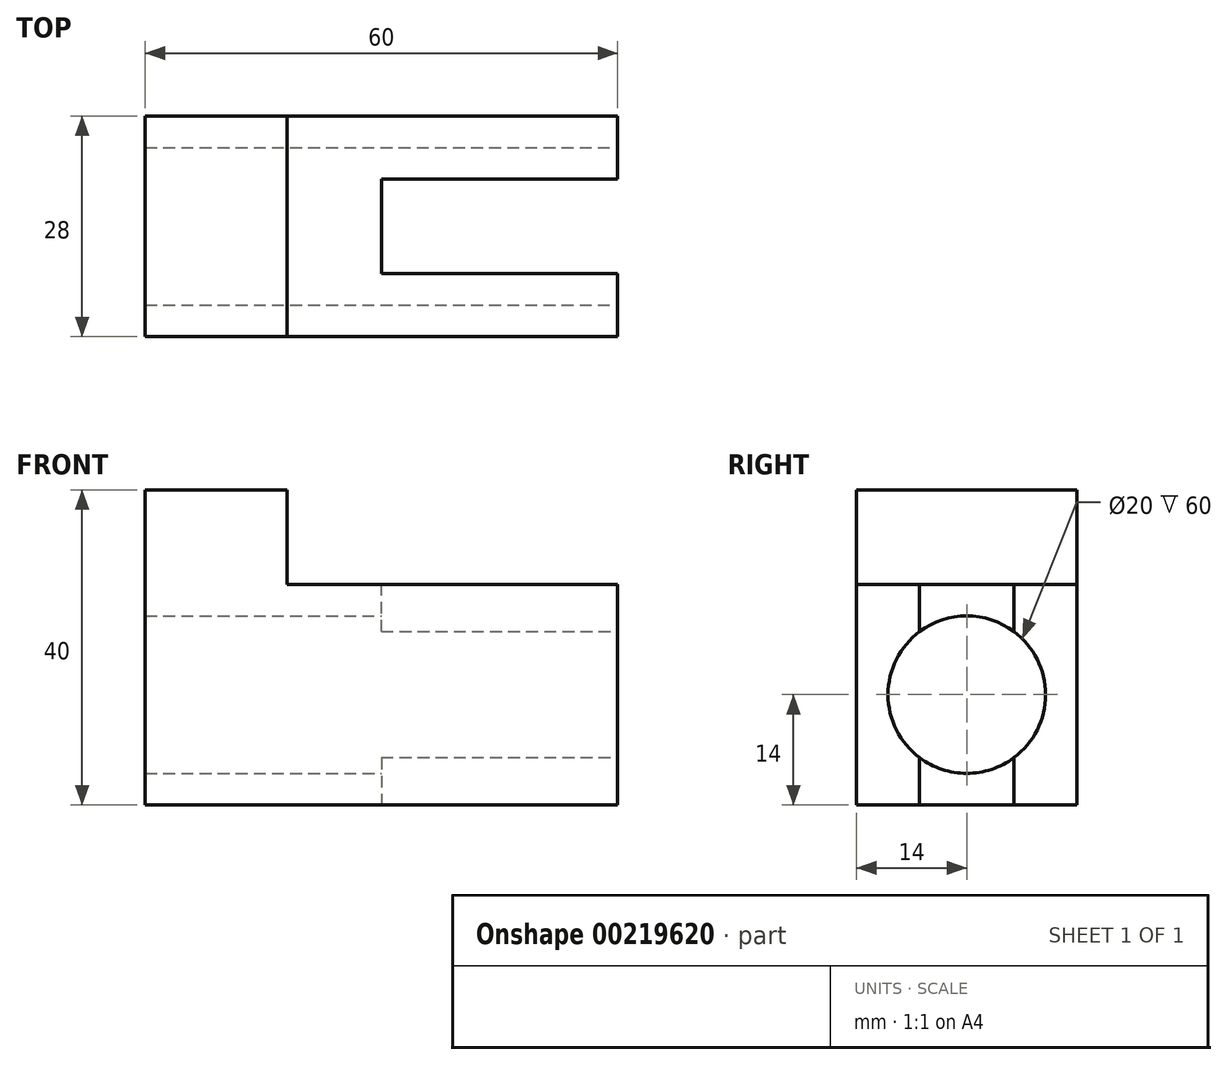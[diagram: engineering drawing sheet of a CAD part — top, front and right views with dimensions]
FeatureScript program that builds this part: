
annotation { "Feature Type Name" : "Feature", "Feature Type Description" : "" }
export const myFeature = defineFeature(function(context is Context, id is Id, definition is map)
    precondition{}
    {
        {
            var Q0;
            Q0=qCreatedBy(makeId("Front.planeOp"),FACE);
            var sketch = newSketch(context, id + "F0", { "sketchPlane" : qUnion([Q0])});
            skLineSegment(sketch, "E0", {"start": v(0, 0) * mm, "end": v(-60, 0) * mm});
            skLineSegment(sketch, "E1", {"start": v(-60, 0) * mm, "end": v(-60, 40) * mm});
            skLineSegment(sketch, "E2", {"start": v(-60, 40) * mm, "end": v(-42, 40) * mm});
            skLineSegment(sketch, "E3", {"start": v(-42, 40) * mm, "end": v(-42, 28) * mm});
            skLineSegment(sketch, "E4", {"start": v(-42, 28) * mm, "end": v(0, 28) * mm});
            skLineSegment(sketch, "E5", {"start": v(0, 28) * mm, "end": v(0, 0) * mm});
            skSolve(sketch);
        }
        {
            var Q0;
            Q0=makeQuery(id+"F0.imprint","IMPRINT",FACE,{"disambiguationData":[TD([[makeQuery(id+"F0.imprint","IMPRINT",EDGE,{"derivedFrom":sQuery(id+"F0.wireOp",EDGE,"E0")}),-1.0]])]});
            extrude(context, id + "F1", {"entities" : qUnion([Q0]), "depth" : 28 * mm});
        }
        {
            var Q0;
            Q0=makeQuery(id+"F1.opExtrude","SWEPT_FACE",FACE,{"disambiguationData":[OSD([sQuery(id+"F0.wireOp",EDGE,"E5")])]});
            var sketch = newSketch(context, id + "F2", { "sketchPlane" : qUnion([Q0])});
            skLineSegment(sketch, "E6", {"start": v(-28, 0) * mm, "end": v(-20, 0) * mm});
            skLineSegment(sketch, "E7", {"start": v(-20, 0) * mm, "end": v(-8, 0) * mm});
            skLineSegment(sketch, "E8", {"start": v(-8, 0) * mm, "end": v(-8, 28) * mm});
            skLineSegment(sketch, "E9", {"start": v(-8, 28) * mm, "end": v(-20, 28) * mm});
            skLineSegment(sketch, "E10", {"start": v(-20, 28) * mm, "end": v(-20, 0) * mm});
            skSolve(sketch);
        }
        {
            var Q0;
            Q0 = qSketchRegion(id + "F2", true);
            extrude(context, id + "F3", {"entities" : qUnion([Q0]), "operationType" : NewBodyOperationType.ADD, "depth" : 25 * mm});
        }
        {
            var Q0;
            Q0=makeQuery(id+"F3.opExtrude","CAP_FACE",FACE,{"disambiguationData":[OSD([sQuery(id+"F2.wireOp",EDGE,"E7"),sQuery(id+"F2.wireOp",EDGE,"E8"),sQuery(id+"F2.wireOp",EDGE,"E9"),sQuery(id+"F2.wireOp",EDGE,"E10")])],"isStart":false});
            extrude(context, id + "F4", {"entities" : qUnion([Q0]), "operationType" : NewBodyOperationType.REMOVE, "oppositeDirection" : true, "depth" : 25 * mm});
        }
        {
            var Q0;
            {var subQ0=sQuery(id+"F2.wireOp",EDGE,"E10");var subQ1=sQuery(id+"F2.wireOp",EDGE,"E9");var subQ2=sQuery(id+"F2.wireOp",EDGE,"E8");var subQ3=sQuery(id+"F2.wireOp",EDGE,"E7");var subQ6=sQuery(id+"F0.wireOp",EDGE,"E5");var subQ14=makeQuery(id+"F1.opExtrude","SWEPT_FACE",FACE,{"disambiguationData":[OSD([subQ6])]});Q0=makeQuery(id+"F4.boolean.opBoolean","MERGE",FACE,{"derivedFrom":[makeQuery(id+"F3.boolean.opBoolean","SPLIT",FACE,{"disambiguationData":[TD([makeQuery(id+"F3.opExtrude","SWEPT_FACE",FACE,{"disambiguationData":[OSD([subQ2])]})])],"derivedFrom":subQ14}),makeQuery(id+"F3.boolean.opBoolean","SPLIT",FACE,{"disambiguationData":[TD([makeQuery(id+"F3.opExtrude","SWEPT_FACE",FACE,{"disambiguationData":[OSD([subQ0])]})])],"derivedFrom":subQ14}),makeQuery(id+"F4.opExtrude","CAP_FACE",FACE,{"disambiguationData":[OSD([subQ3,subQ2,subQ1,subQ0])],"isStart":false})]});}
            var sketch = newSketch(context, id + "F5", { "sketchPlane" : qUnion([Q0])});
            skLineSegment(sketch, "E11", {"start": v(-28, 0) * mm, "end": v(-20, 0) * mm});
            skLineSegment(sketch, "E12", {"start": v(-20, 0) * mm, "end": v(-8, 0) * mm});
            skLineSegment(sketch, "E13", {"start": v(-8, 0) * mm, "end": v(-8, 28) * mm});
            skLineSegment(sketch, "E14", {"start": v(-8, 28) * mm, "end": v(-20, 28) * mm});
            skLineSegment(sketch, "E15", {"start": v(-20, 28) * mm, "end": v(-20, 0) * mm});
            skSolve(sketch);
        }
        {
            var Q0;
            Q0=makeQuery(id+"F5.imprint","IMPRINT",FACE,{"disambiguationData":[TD([[makeQuery(id+"F5.imprint","IMPRINT",EDGE,{"derivedFrom":sQuery(id+"F5.wireOp",EDGE,"E12")}),1.0]])]});
            extrude(context, id + "F6", {"entities" : qUnion([Q0]), "operationType" : NewBodyOperationType.REMOVE, "oppositeDirection" : true, "depth" : 30 * mm});
        }
        {
            var Q0;
            {var subQ2=sQuery(id+"F0.wireOp",EDGE,"E5");var subQ8=sQuery(id+"F2.wireOp",EDGE,"E7");var subQ11=sQuery(id+"F2.wireOp",EDGE,"E9");var subQ13=sQuery(id+"F2.wireOp",EDGE,"E10");var subQ14=sQuery(id+"F2.wireOp",EDGE,"E8");var subQ15=makeQuery(id+"F1.opExtrude","SWEPT_FACE",FACE,{"disambiguationData":[OSD([subQ2])]});Q0=makeQuery(id+"F6.boolean.opBoolean","SPLIT",FACE,{"disambiguationData":[TD([makeQuery(id+"F6.opExtrude","SWEPT_FACE",FACE,{"disambiguationData":[OSD([sQuery(id+"F5.wireOp",EDGE,"E15")])]})])],"derivedFrom":makeQuery(id+"F4.boolean.opBoolean","MERGE",FACE,{"derivedFrom":[makeQuery(id+"F3.boolean.opBoolean","SPLIT",FACE,{"disambiguationData":[TD([makeQuery(id+"F3.opExtrude","SWEPT_FACE",FACE,{"disambiguationData":[OSD([subQ14])]})])],"derivedFrom":subQ15}),makeQuery(id+"F3.boolean.opBoolean","SPLIT",FACE,{"disambiguationData":[TD([makeQuery(id+"F3.opExtrude","SWEPT_FACE",FACE,{"disambiguationData":[OSD([subQ13])]})])],"derivedFrom":subQ15}),makeQuery(id+"F4.opExtrude","CAP_FACE",FACE,{"disambiguationData":[OSD([subQ8,subQ14,subQ11,subQ13])],"isStart":false})]})});}
            var sketch = newSketch(context, id + "F7", { "sketchPlane" : qUnion([Q0])});
            skLineSegment(sketch, "E16", {"start": v(-28, 14) * mm, "end": v(-14, 14) * mm});
            skCircle(sketch, "E17", {"center": v(-14, 14) * mm, "radius": 10 * mm});
            skSolve(sketch);
        }
        {
            var Q0;
            {var subQ0=sQuery(id+"F7.wireOp",EDGE,"E17");var subQ1=makeQuery(id+"F6.boolean.opBoolean","COPY",EDGE,{"derivedFrom":makeQuery(id+"F6.opExtrude","CAP_EDGE",EDGE,{"disambiguationData":[OSD([sQuery(id+"F5.wireOp",EDGE,"E15")])],"isStart":true})});var subQ2=makeQuery(id+"F7.imprint","INTERSECT",VERTEX,{"disambiguationData":[OD(0.0)],"derivedFrom":[subQ1,subQ0]});Q0=makeQuery(id+"F7.imprint","IMPRINT",FACE,{"disambiguationData":[TD([[makeQuery(id+"F7.imprint","IMPRINT",EDGE,{"disambiguationData":[TD([[subQ2,1.0]])],"derivedFrom":subQ0}),1.0]])]});}
            var Q1;
            {var subQ0=sQuery(id+"F7.wireOp",EDGE,"E17");var subQ1=sQuery(id+"F7.wireOp",EDGE,"E16");var subQ2=makeQuery(id+"F7.imprint","INTERSECT",VERTEX,{"derivedFrom":[subQ1,subQ0]});Q1=makeQuery(id+"F7.imprint","IMPRINT",FACE,{"disambiguationData":[TD([[makeQuery(id+"F7.imprint","IMPRINT",EDGE,{"disambiguationData":[TD([[subQ2,-1.0]])],"derivedFrom":subQ1}),-1.0]])]});}
            var Q2;
            {var subQ0=sQuery(id+"F7.wireOp",EDGE,"E17");var subQ1=sQuery(id+"F7.wireOp",EDGE,"E16");var subQ2=makeQuery(id+"F7.imprint","INTERSECT",VERTEX,{"derivedFrom":[subQ1,subQ0]});Q2=makeQuery(id+"F7.imprint","IMPRINT",FACE,{"disambiguationData":[TD([[makeQuery(id+"F7.imprint","IMPRINT",EDGE,{"disambiguationData":[TD([[subQ2,-1.0]])],"derivedFrom":subQ1}),1.0]])]});}
            extrude(context, id + "F8", {"entities" : qUnion([Q0, Q1, Q2]), "operationType" : NewBodyOperationType.REMOVE, "oppositeDirection" : true, "depth" : 60 * mm});
        }
    });
